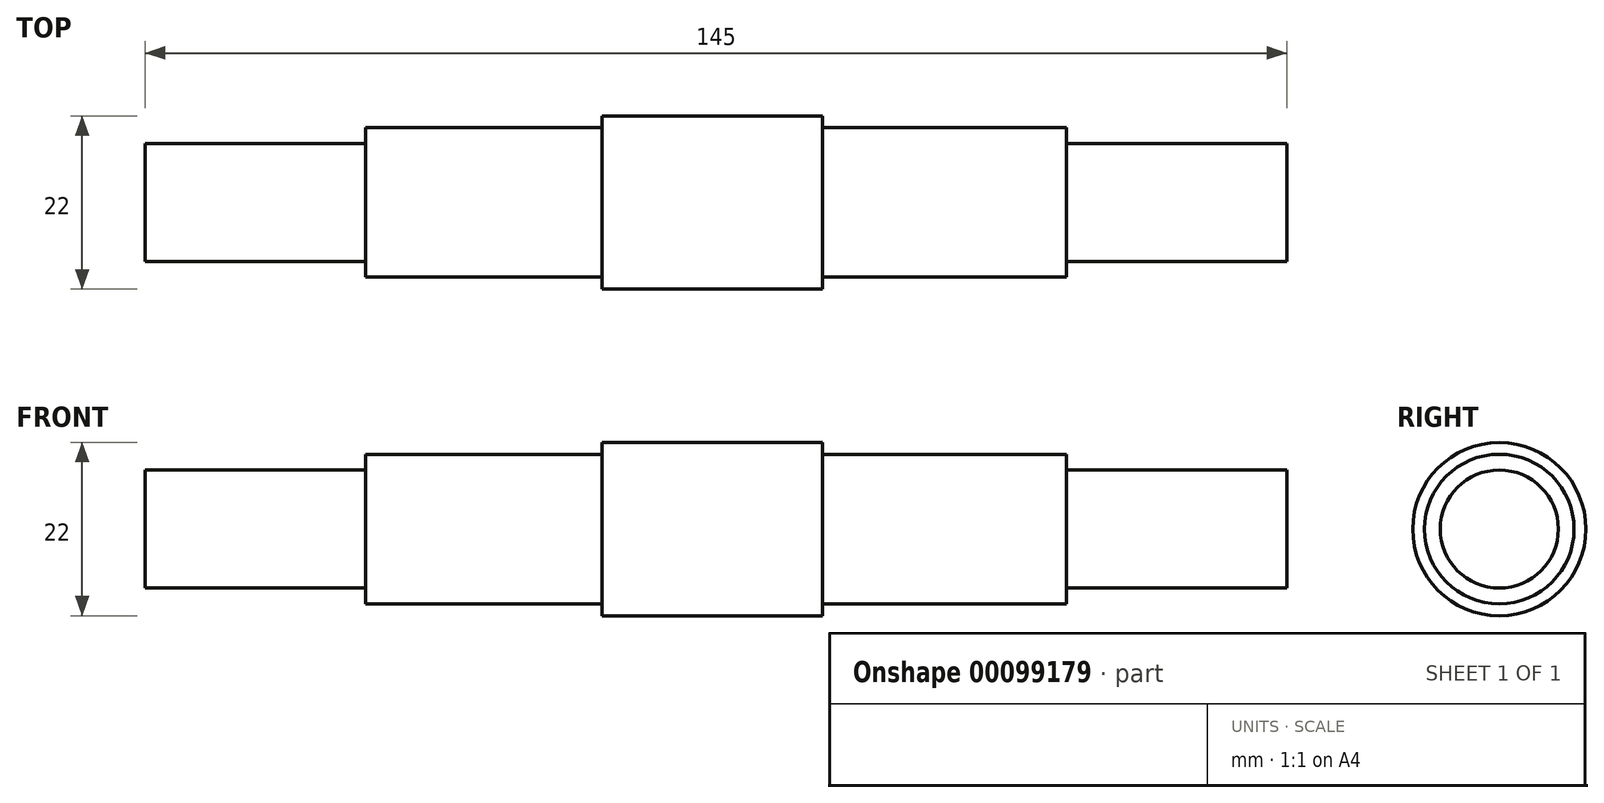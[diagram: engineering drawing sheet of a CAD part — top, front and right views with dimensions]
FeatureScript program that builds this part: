
annotation { "Feature Type Name" : "Feature", "Feature Type Description" : "" }
export const myFeature = defineFeature(function(context is Context, id is Id, definition is map)
    precondition{}
    {
        {
            var Q0;
            Q0=qCreatedBy(makeId("Front.planeOp"),FACE);
            var sketch = newSketch(context, id + "F0", { "sketchPlane" : qUnion([Q0])});
            skLineSegment(sketch, "E0", {"start": v(-47.67, 0) * mm, "end": v(-47.67, 7.5) * mm});
            skLineSegment(sketch, "E1", {"start": v(-47.67, 7.5) * mm, "end": v(-19.67, 7.5) * mm});
            skLineSegment(sketch, "E2", {"start": v(-19.67, 7.5) * mm, "end": v(-19.67, 9.5) * mm});
            skLineSegment(sketch, "E3", {"start": v(-19.67, 9.5) * mm, "end": v(10.33, 9.5) * mm});
            skLineSegment(sketch, "E4", {"start": v(10.33, 9.5) * mm, "end": v(10.33, 11) * mm});
            skLineSegment(sketch, "E5", {"start": v(10.33, 11) * mm, "end": v(38.33, 11) * mm});
            skLineSegment(sketch, "E6", {"start": v(38.33, 11) * mm, "end": v(38.33, 9.5) * mm});
            skLineSegment(sketch, "E7", {"start": v(38.33, 9.5) * mm, "end": v(69.33, 9.5) * mm});
            skLineSegment(sketch, "E8", {"start": v(69.33, 9.5) * mm, "end": v(69.33, 7.5) * mm});
            skLineSegment(sketch, "E9", {"start": v(69.33, 7.5) * mm, "end": v(97.33, 7.5) * mm});
            skLineSegment(sketch, "E10", {"start": v(97.33, 7.5) * mm, "end": v(97.33, 0) * mm});
            skLineSegment(sketch, "E11", {"start": v(97.33, 0) * mm, "end": v(-47.67, 0) * mm});
            skSolve(sketch);
        }
        {
            var Q0;
            Q0=makeQuery(id+"F0.imprint","IMPRINT",FACE,{"disambiguationData":[TD([[makeQuery(id+"F0.imprint","IMPRINT",EDGE,{"derivedFrom":sQuery(id+"F0.wireOp",EDGE,"E0")}),-1.0]])]});
            var Q1;
            Q1=sQuery(id+"F0.wireOp",EDGE,"E11");
            revolve(context, id + "F1", {"entities" : qUnion([Q0]), "axis" : qUnion([Q1]), "revolveType" : RevolveType.FULL});
        }
    });
